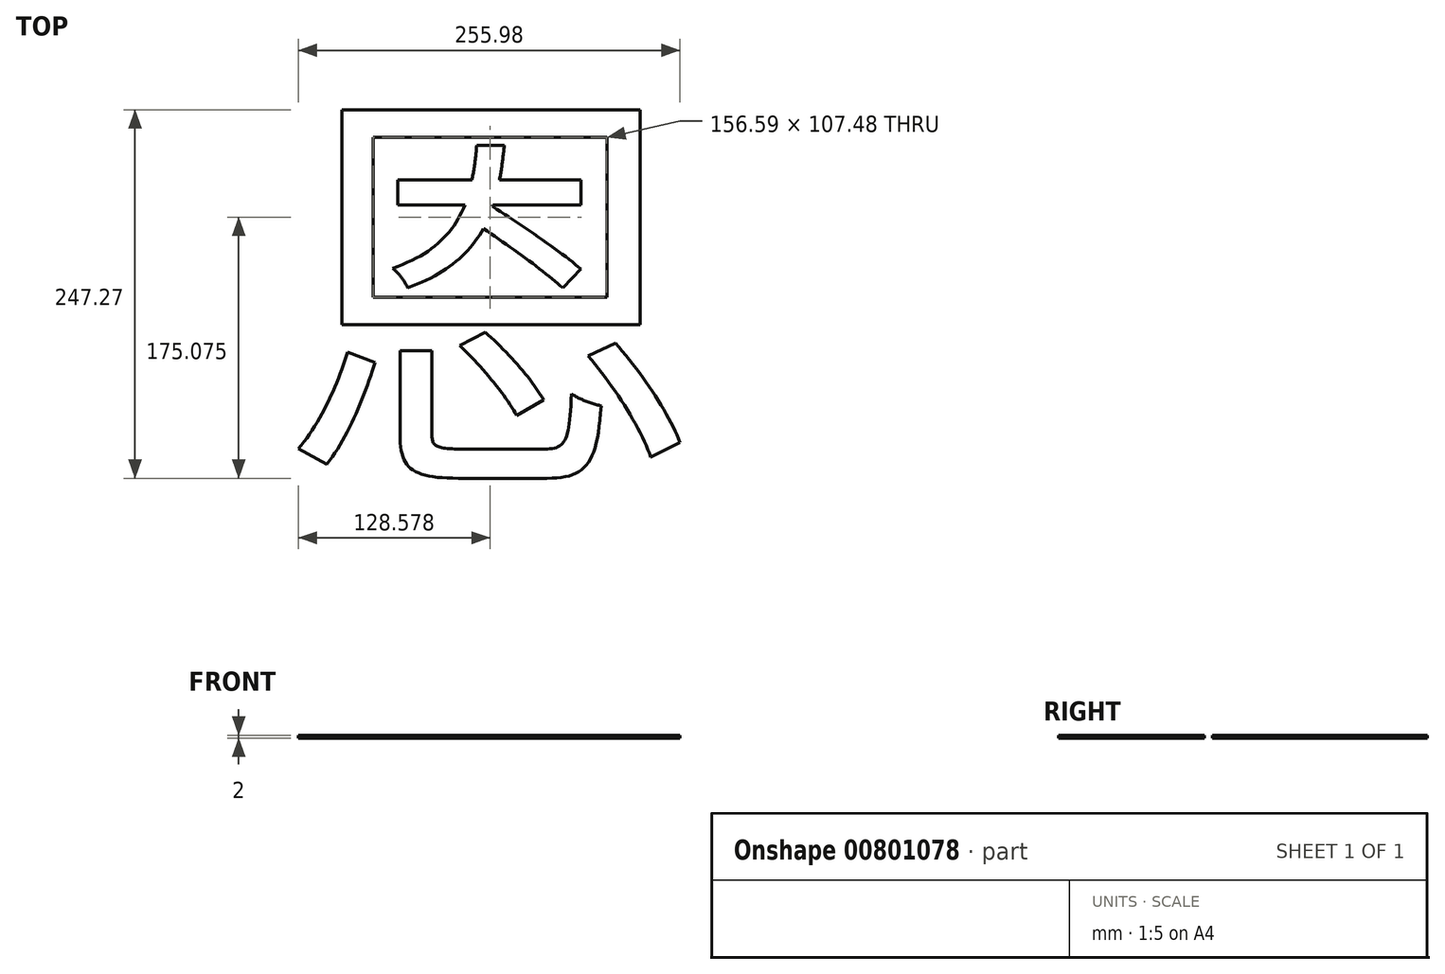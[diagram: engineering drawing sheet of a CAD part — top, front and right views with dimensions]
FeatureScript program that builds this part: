
annotation { "Feature Type Name" : "Feature", "Feature Type Description" : "" }
export const myFeature = defineFeature(function(context is Context, id is Id, definition is map)
    precondition{}
    {
        {
            var Q0;
            Q0=qCreatedBy(makeId("Top.planeOp"),FACE);
            var sketch = newSketch(context, id + "F0", { "sketchPlane" : qUnion([Q0])});
            skText(sketch, "E0", { "text": "恩", "fontName": "NotoSansCJKtc-Regular.otf"});
            const initialGuessF0  = {"E0": [0, 0, 1, 0, 0.208]};
            skSetInitialGuess(sketch, initialGuessF0);
            skSolve(sketch);
        }
        {
            var Q0;
            Q0 = qSketchRegion(id + "F0", true);
            var Q1;
            Q1=makeQuery(id+"F0.imprint","IMPRINT",FACE,{"disambiguationData":[TD([[makeQuery(id+"F0.imprint","IMPRINT",EDGE,{"derivedFrom":sQuery(id+"F0.wireOp",EDGE,"E0.sketch_text.stroke-0")}),1.0]])]});
            extrude(context, id + "F1", {"entities" : qUnion([Q0, Q1]), "depth" : 2 * mm, "offsetDistance" : 25.4 * mm});
        }
    });
